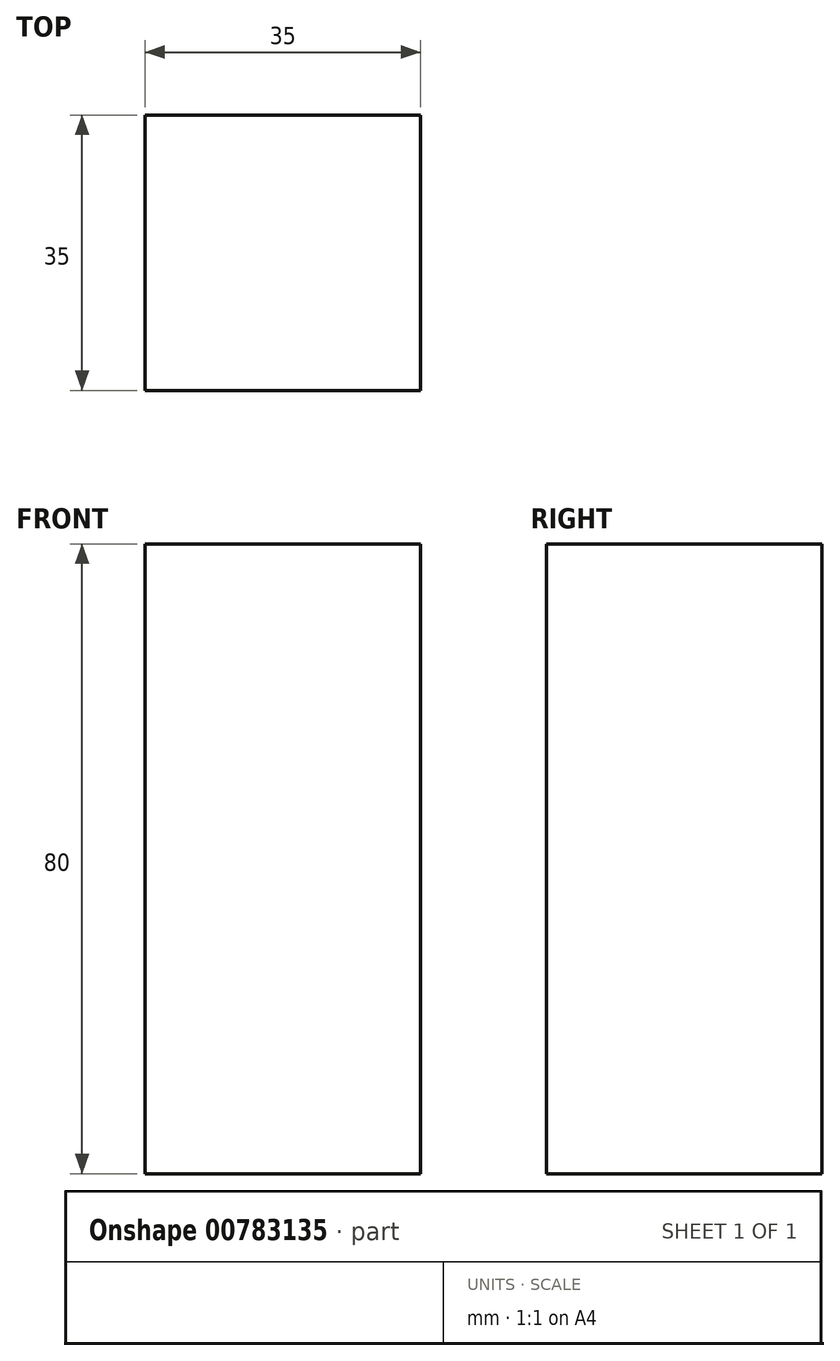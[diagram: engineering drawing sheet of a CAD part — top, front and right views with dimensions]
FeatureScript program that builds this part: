
annotation { "Feature Type Name" : "Feature", "Feature Type Description" : "" }
export const myFeature = defineFeature(function(context is Context, id is Id, definition is map)
    precondition{}
    {
        {
            var Q0;
            Q0=qCreatedBy(makeId("Top.planeOp"),FACE);
            var sketch = newSketch(context, id + "F0", { "sketchPlane" : qUnion([Q0])});
            skLineSegment(sketch, "E0.bottom", {"start": v(-17.5, 17.5) * mm, "end": v(17.5, 17.5) * mm});
            skLineSegment(sketch, "E0.top", {"start": v(-17.5, -17.5) * mm, "end": v(17.5, -17.5) * mm});
            skLineSegment(sketch, "E0.left", {"start": v(-17.5, 17.5) * mm, "end": v(-17.5, -17.5) * mm});
            skLineSegment(sketch, "E0.right", {"start": v(17.5, 17.5) * mm, "end": v(17.5, -17.5) * mm});
            skPoint(sketch, "E0.middle", {"position": v(0, 0) * mm});
            skSolve(sketch);
        }
        {
            var Q0;
            Q0=makeQuery(id+"F0.imprint","IMPRINT",FACE,{"disambiguationData":[TD([[makeQuery(id+"F0.imprint","IMPRINT",EDGE,{"derivedFrom":sQuery(id+"F0.wireOp",EDGE,"E0.bottom")}),-1.0]])]});
            extrude(context, id + "F1", {"entities" : qUnion([Q0]), "depth" : 80 * mm, "offsetDistance" : 25 * mm});
        }
    });
